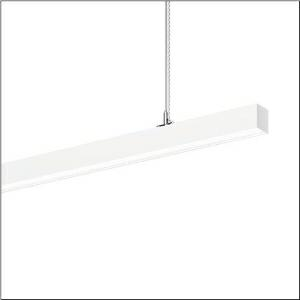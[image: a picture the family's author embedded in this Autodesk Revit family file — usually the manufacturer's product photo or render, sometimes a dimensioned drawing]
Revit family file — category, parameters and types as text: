
# Revit family: silica_21_51mx33da47wb
name_source: partatom
category: Lighting Fixtures
units: mm (PartAtom-declared; Revit-internal decimal feet)

## family parameters
Cut with Voids When Loaded = No
Host = Face
Light Source = No
Part Type = Normal
Room Calculation Point = No
Round Connector Dimension = Use Diameter
Shared = No

## types (1)
- --- (1 x LED, 5910 lm, 38.4 W, 4000K)
    Apparent Load = 38 VA
    CIE Flux Codes = 78 96 99 55 100
    Color Rendering = 80
    Color Temperature = 4000K
    Default Elevation = 1800 mm
    Description = Silica 21, office luminaire, primary optical cover: prismatic diffuser, of PMMA, CAT 2 (L<= 3000cd/m²), light emission: direct/indirect distribution, primary light characteristic: symmetric, installation type: suspended mounting, LED, rated luminous flux: 5.910lm, luminous efficacy: 154lm/W, light colour: 840, colour temperature: 4000K, control gear: DALI 2, with terminal, 3+2-pole, max. 2.5mm², mains connection: 220..240V, AC, 50/60Hz, rated input power: 38.4W, luminaire housing, of aluminium, traffic white (RAL 9016), length: 1.204mm, width: 53mm, height: 53mm, protection rating (complete): IP20, insulation class (complete): insulation class I (protective earthing), certification: CE, permissible operating ambient temperature: 0..+35°C, standard: EN 50419, packaging unit: 1 piece
    Height = 53 mm
    Lamp = 1 x LED
    Lamp Light Flux = 5910 lm
    Lamp Power = 38.4 W
    Lamp count = 1
    Length = 1204 mm
    Luminous efficacy = 154 lm/W
    Manufacturer = Siteco
    ModVariant = No
    Model = 51MX33DA47WB
    Mounting Place = Ceiling
    Mounting Type = Pendant
    Number of Poles = 1
    OnlyDefault = Yes
    Power Factor = 1
    Product Name = Silica 21
    Product group = office luminaire | ceiling pendant
    ProductGroupID = 903
    Protection Class = Protection class I
    Protection Degree = IP 20
    RLX_Detail_Level = 1
    RLX_Emergency_Light_Flux = 0 lm
    RLX_Emergency_Type = 0
    RLX_Emergency_Type_DB = No
    RlxData = <blob elided: 21197 chars, md5=a33c9b03>
    Socket = socket
    Standby Power = 0 W
    System Light Flux = 5910 lm
    System Power = 38 W
    Type Comments = factory setting: luminous flux: 100 % | dim-lin: 254 | 322 mA
    Type Image = l_1349007.jpg
    URL = http://relux.com
    VarID = @adj_119087
    Voltage = 0 V
    Weight = 0.00 kg
    Width = 53 mm

## geometry (parser evidence)
native form markers: Blend x4, Sweep x11
no freeform markers — native parametric forms only
